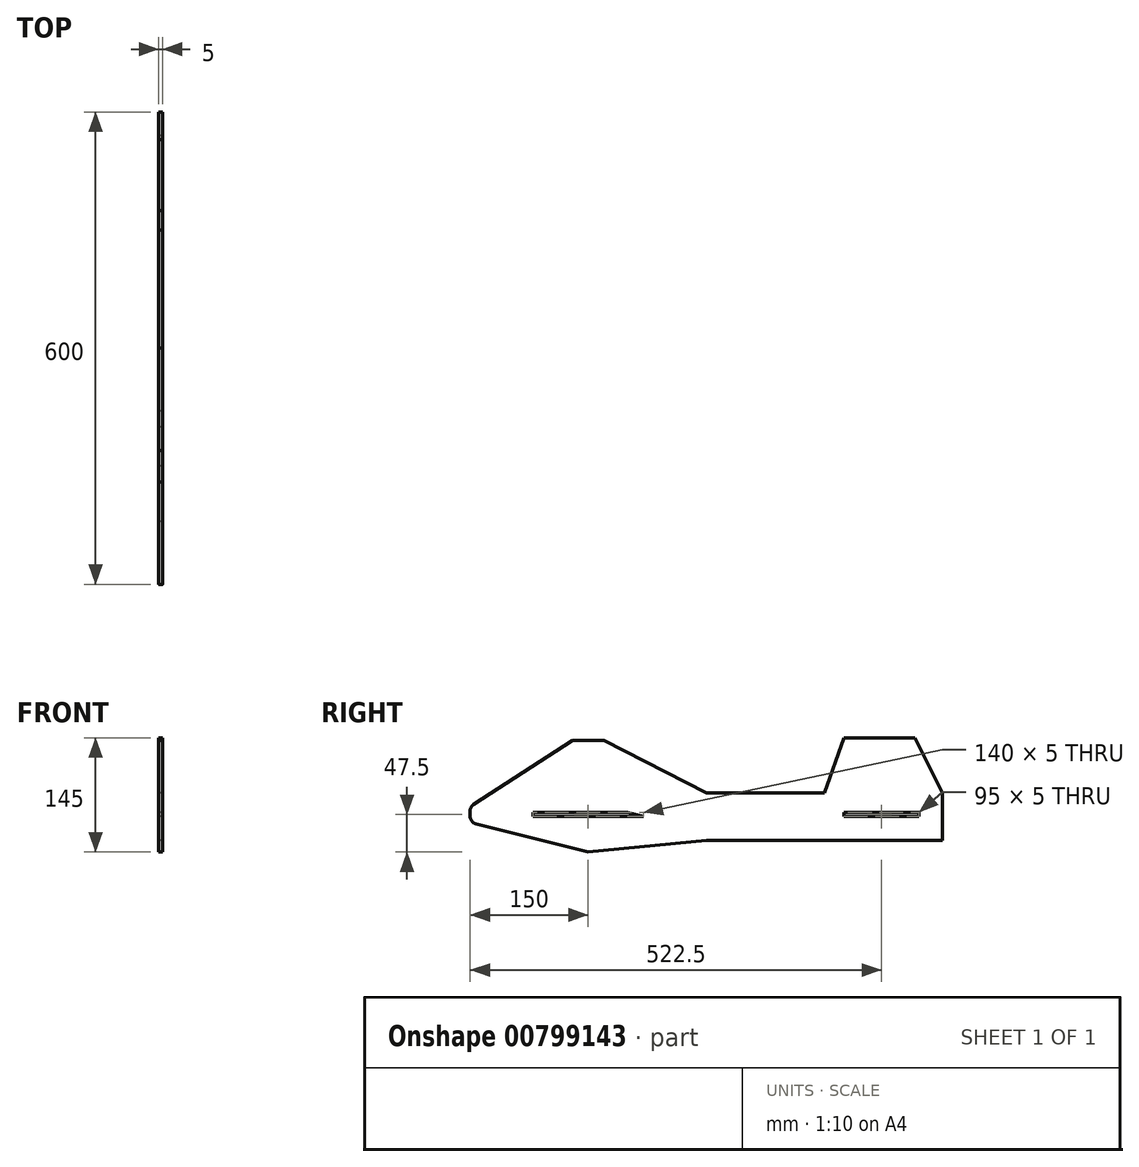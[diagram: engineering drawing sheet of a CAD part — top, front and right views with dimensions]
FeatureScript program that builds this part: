
annotation { "Feature Type Name" : "Feature", "Feature Type Description" : "" }
export const myFeature = defineFeature(function(context is Context, id is Id, definition is map)
    precondition{}
    {
        {
            var Q0;
            Q0=qCreatedBy(makeId("Right.planeOp"),FACE);
            var sketch = newSketch(context, id + "F0", { "sketchPlane" : qUnion([Q0])});
            skLineSegment(sketch, "E0", {"start": v(0, 0) * mm, "end": v(-300, 0) * mm, "construction": true});
            skLineSegment(sketch, "E1", {"start": v(0, 0) * mm, "end": v(300, 0) * mm, "construction": true});
            skLineSegment(sketch, "E2", {"start": v(-300, 0) * mm, "end": v(-300, 10) * mm});
            skLineSegment(sketch, "E3", {"start": v(-300, 0) * mm, "end": v(-300, -10) * mm});
            skLineSegment(sketch, "E4", {"start": v(-220, 0) * mm, "end": v(-220, 2.5) * mm});
            skLineSegment(sketch, "E5", {"start": v(-220, 0) * mm, "end": v(-220, -2.5) * mm});
            skLineSegment(sketch, "E6", {"start": v(-220, -2.5) * mm, "end": v(-80, -2.5) * mm});
            skLineSegment(sketch, "E7", {"start": v(-80, -2.5) * mm, "end": v(-80, 2.5) * mm});
            skLineSegment(sketch, "E8", {"start": v(-80, 2.5) * mm, "end": v(-220, 2.5) * mm});
            skLineSegment(sketch, "E9", {"start": v(-150, 2.5) * mm, "end": v(-150, 94.5) * mm, "construction": true});
            skLineSegment(sketch, "E10", {"start": v(-150, 94.5) * mm, "end": v(-170, 94.5) * mm});
            skLineSegment(sketch, "E11", {"start": v(-150, 94.5) * mm, "end": v(-130, 94.5) * mm});
            skLineSegment(sketch, "E12", {"start": v(-170, 94.5) * mm, "end": v(-300, 10) * mm});
            skLineSegment(sketch, "E13", {"start": v(-150, -2.5) * mm, "end": v(-150, -47.5) * mm, "construction": true});
            skLineSegment(sketch, "E14", {"start": v(-300, -10) * mm, "end": v(-150, -47.5) * mm});
            skLineSegment(sketch, "E15", {"start": v(270, 0) * mm, "end": v(270, 2.5) * mm});
            skLineSegment(sketch, "E16", {"start": v(270, 0) * mm, "end": v(270, -2.5) * mm});
            skLineSegment(sketch, "E17", {"start": v(270, -2.5) * mm, "end": v(175, -2.5) * mm});
            skLineSegment(sketch, "E18", {"start": v(175, -2.5) * mm, "end": v(175, 2.5) * mm});
            skLineSegment(sketch, "E19", {"start": v(175, 2.5) * mm, "end": v(270, 2.5) * mm});
            skLineSegment(sketch, "E20", {"start": v(300, -32.5) * mm, "end": v(300, 27.5) * mm});
            skLineSegment(sketch, "E21", {"start": v(300, -32.5) * mm, "end": v(0, -32.5) * mm});
            skLineSegment(sketch, "E22", {"start": v(-150, -47.5) * mm, "end": v(0, -32.5) * mm});
            skPoint(sketch, "E23", {"position": v(300, 27.5) * mm});
            skPoint(sketch, "E24", {"position": v(150, 27.5) * mm});
            skPoint(sketch, "E25", {"position": v(265, 2.5) * mm});
            skLineSegment(sketch, "E26", {"start": v(265, 2.5) * mm, "end": v(265, 97.5) * mm, "construction": true});
            skLineSegment(sketch, "E27", {"start": v(265, 97.5) * mm, "end": v(175, 97.5) * mm});
            skLineSegment(sketch, "E28", {"start": v(175, 97.5) * mm, "end": v(150, 27.5) * mm});
            skLineSegment(sketch, "E29", {"start": v(265, 97.5) * mm, "end": v(300, 27.5) * mm});
            skLineSegment(sketch, "E30", {"start": v(150, 27.5) * mm, "end": v(0, 27.5) * mm});
            skLineSegment(sketch, "E31", {"start": v(0, 27.5) * mm, "end": v(-130, 94.5) * mm});
            skLineSegment(sketch, "E32", {"start": v(-80, -2.5) * mm, "end": v(-100, 2.5) * mm});
            skPoint(sketch, "E33", {"position": v(-100, 2.5) * mm});
            skSolve(sketch);
        }
        {
            var Q0;
            Q0=makeQuery(id+"F0.imprint","IMPRINT",FACE,{"disambiguationData":[TD([[makeQuery(id+"F0.imprint","IMPRINT",EDGE,{"derivedFrom":sQuery(id+"F0.wireOp",EDGE,"E2")}),-1.0]])]});
            var Q1;
            {var subQ0=sQuery(id+"F0.wireOp",EDGE,"E7");Q1=makeQuery(id+"F0.imprint","IMPRINT",FACE,{"disambiguationData":[TD([[makeQuery(id+"F0.imprint","IMPRINT",EDGE,{"derivedFrom":subQ0}),1.0]])]});}
            extrude(context, id + "F1", {"entities" : qUnion([Q0, Q1]), "endBound" : BoundingType.SYMMETRIC, "depth" : 5 * mm, "offsetDistance" : 25 * mm});
        }
        {
            var Q0;
            Q0=makeQuery(id+"F1.opExtrude","SWEPT_EDGE",EDGE,{"disambiguationData":[OSD([sQuery(id+"F0.wireOp",EDGE,"E2"),sQuery(id+"F0.wireOp",EDGE,"E12")])]});
            fillet(context, id + "F2", {"entities" : qUnion([Q0]), "radius" : 10 * mm, "tangentPropagation" : true, "allowEdgeOverflow" : false});
        }
        {
            var Q0;
            Q0=makeQuery(id+"F1.opExtrude","SWEPT_EDGE",EDGE,{"disambiguationData":[OSD([sQuery(id+"F0.wireOp",EDGE,"E3"),sQuery(id+"F0.wireOp",EDGE,"E14")])]});
            fillet(context, id + "F3", {"entities" : qUnion([Q0]), "radius" : 10 * mm, "tangentPropagation" : true, "allowEdgeOverflow" : false});
        }
    });
